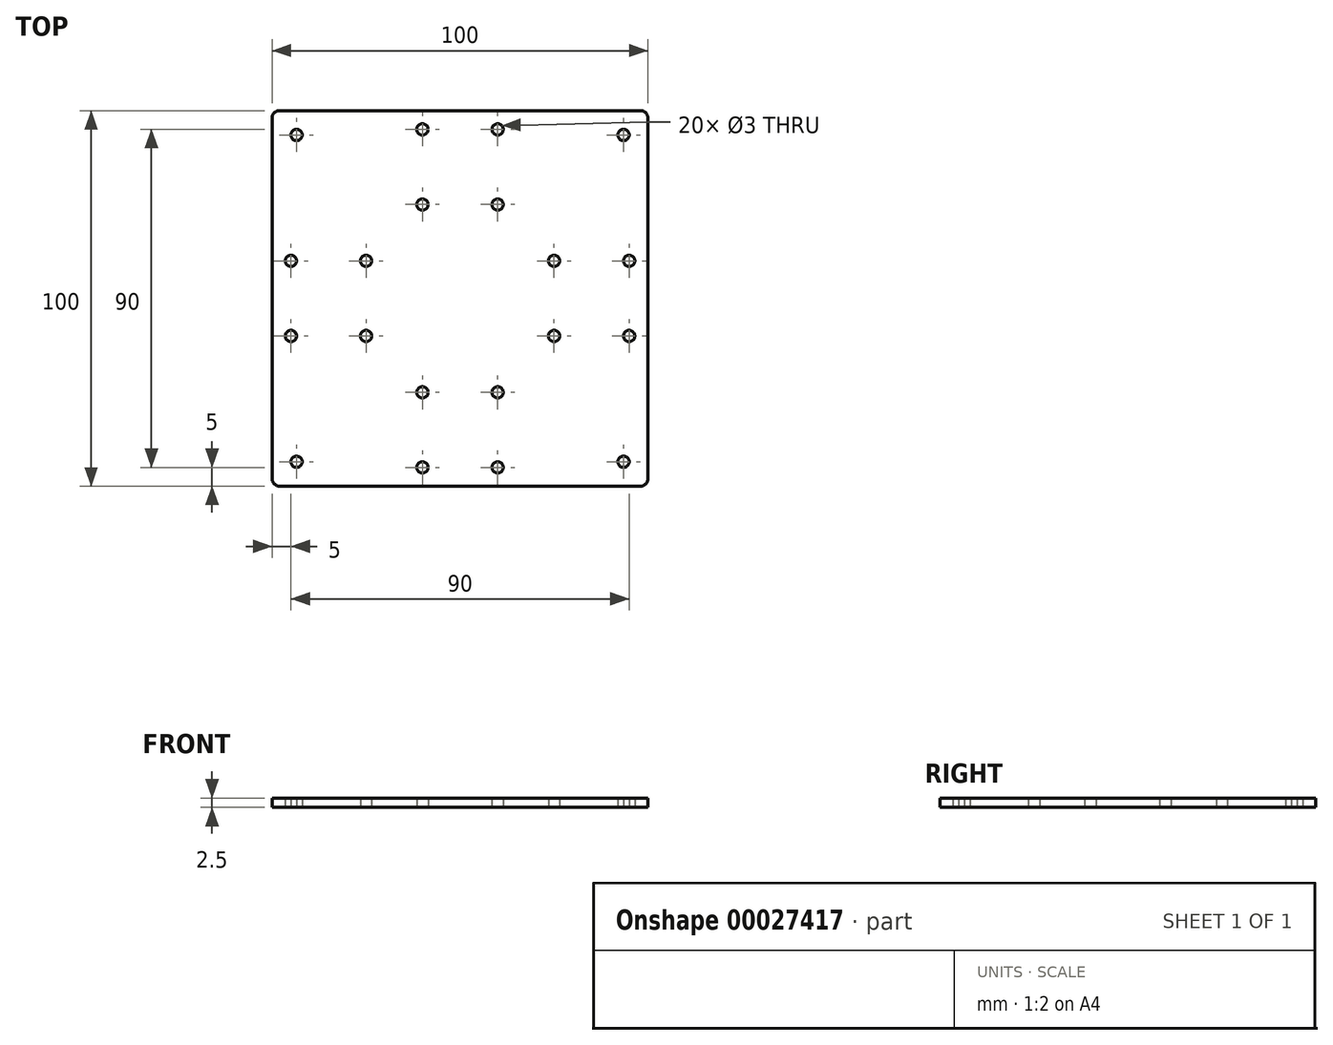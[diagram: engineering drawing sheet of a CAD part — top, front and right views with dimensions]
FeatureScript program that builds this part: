
annotation { "Feature Type Name" : "Feature", "Feature Type Description" : "" }
export const myFeature = defineFeature(function(context is Context, id is Id, definition is map)
    precondition{}
    {
        {
            var Q0;
            Q0=qCreatedBy(makeId("Top.planeOp"),FACE);
            var sketch = newSketch(context, id + "F0", { "sketchPlane" : qUnion([Q0])});
            skLineSegment(sketch, "E0.rect.bottom", {"start": v(50, -50) * mm, "end": v(-50, -50) * mm});
            skLineSegment(sketch, "E0.rect.top", {"start": v(50, 50) * mm, "end": v(-50, 50) * mm});
            skLineSegment(sketch, "E0.rect.left", {"start": v(50, -50) * mm, "end": v(50, 50) * mm});
            skLineSegment(sketch, "E0.rect.right", {"start": v(-50, -50) * mm, "end": v(-50, 50) * mm});
            skPoint(sketch, "E0.rect.middle", {"position": v(0, 0) * mm});
            skLineSegment(sketch, "E1", {"start": v(50, 45) * mm, "end": v(-50, 45) * mm, "construction": true});
            skCircle(sketch, "E2", {"center": v(-10, 45) * mm, "radius": 1.5 * mm});
            skCircle(sketch, "E3", {"center": v(10, 45) * mm, "radius": 1.5 * mm});
            skLineSegment(sketch, "E4", {"start": v(-50, 0) * mm, "end": v(50, 0) * mm, "construction": true});
            skCircle(sketch, "E5.MirrorC", {"center": v(-10, -45) * mm, "radius": 1.5 * mm});
            skCircle(sketch, "E6.MirrorC", {"center": v(10, -45) * mm, "radius": 1.5 * mm});
            skLineSegment(sketch, "E7", {"start": v(45, 50) * mm, "end": v(45, -50) * mm, "construction": true});
            skCircle(sketch, "E8", {"center": v(45, 10) * mm, "radius": 1.5 * mm});
            skCircle(sketch, "E9.MirrorC", {"center": v(45, -10) * mm, "radius": 1.5 * mm});
            skLineSegment(sketch, "E10", {"start": v(0, 50) * mm, "end": v(0, -50) * mm, "construction": true});
            skCircle(sketch, "E11.MirrorC", {"center": v(-45, 10) * mm, "radius": 1.5 * mm});
            skCircle(sketch, "E12.MirrorC", {"center": v(-45, -10) * mm, "radius": 1.5 * mm});
            skCircle(sketch, "E13", {"center": v(-43.5, -43.5) * mm, "radius": 1.5 * mm});
            skCircle(sketch, "E14.MirrorC", {"center": v(43.5, -43.5) * mm, "radius": 1.5 * mm});
            skCircle(sketch, "E15.MirrorC", {"center": v(43.5, 43.5) * mm, "radius": 1.5 * mm});
            skCircle(sketch, "E16.MirrorC", {"center": v(-43.5, 43.5) * mm, "radius": 1.5 * mm});
            skCircle(sketch, "E17", {"center": v(-10, 25) * mm, "radius": 1.5 * mm});
            skCircle(sketch, "E18", {"center": v(10, 25) * mm, "radius": 1.5 * mm});
            skCircle(sketch, "E19.MirrorC", {"center": v(-10, -25) * mm, "radius": 1.5 * mm});
            skCircle(sketch, "E20.MirrorC", {"center": v(10, -25) * mm, "radius": 1.5 * mm});
            skCircle(sketch, "E21", {"center": v(-25, 10) * mm, "radius": 1.5 * mm});
            skCircle(sketch, "E22", {"center": v(-25, -10) * mm, "radius": 1.5 * mm});
            skCircle(sketch, "E23.MirrorC", {"center": v(25, 10) * mm, "radius": 1.5 * mm});
            skCircle(sketch, "E24.MirrorC", {"center": v(25, -10) * mm, "radius": 1.5 * mm});
            skSolve(sketch);
        }
        {
            var Q0;
            Q0=makeQuery(id+"F0.imprint","IMPRINT",FACE,{"disambiguationData":[TD([[makeQuery(id+"F0.imprint","IMPRINT",EDGE,{"derivedFrom":sQuery(id+"F0.wireOp",EDGE,"E0.rect.bottom")}),-1.0]])]});
            extrude(context, id + "F1", {"entities" : qUnion([Q0]), "depth" : 2.5 * mm});
        }
        {
            var Q0;
            Q0=makeQuery(id+"F1.opExtrude","SWEPT_EDGE",EDGE,{"disambiguationData":[OSD([sQuery(id+"F0.wireOp",EDGE,"E0.rect.bottom"),sQuery(id+"F0.wireOp",EDGE,"E0.rect.left")])]});
            var Q1;
            Q1=makeQuery(id+"F1.opExtrude","SWEPT_EDGE",EDGE,{"disambiguationData":[OSD([sQuery(id+"F0.wireOp",EDGE,"E0.rect.top"),sQuery(id+"F0.wireOp",EDGE,"E0.rect.left")])]});
            var Q2;
            Q2=makeQuery(id+"F1.opExtrude","SWEPT_EDGE",EDGE,{"disambiguationData":[OSD([sQuery(id+"F0.wireOp",EDGE,"E0.rect.top"),sQuery(id+"F0.wireOp",EDGE,"E0.rect.right")])]});
            var Q3;
            Q3=makeQuery(id+"F1.opExtrude","SWEPT_EDGE",EDGE,{"disambiguationData":[OSD([sQuery(id+"F0.wireOp",EDGE,"E0.rect.bottom"),sQuery(id+"F0.wireOp",EDGE,"E0.rect.right")])]});
            fillet(context, id + "F2", {"entities" : qUnion([Q0, Q1, Q2, Q3]), "radius" : 2 * mm, "tangentPropagation" : true, "allowEdgeOverflow" : false});
        }
    });
